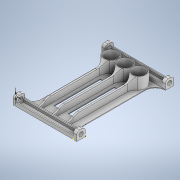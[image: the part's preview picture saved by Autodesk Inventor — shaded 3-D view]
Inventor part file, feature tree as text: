
AUTODESK INVENTOR PART (.ipt)
format: ipt  version: 2020 (Build 240168000, 168)  size: 441,856 bytes
history: native  units: mm
features: sketch x21, extrude x18, fillet x7
ambient origin geometry x8: Origin, YZ Plane, XZ Plane, XY Plane, X Axis, Y Axis, Z Axis, Center Point
bodies: Solid1 (feature_tree)
feature tree (46):
  extrude  "Extrusion1"  Depth=25.4mm
  extrude  "Extrusion2"  Depth=10.0mm TaperAngle=0.0deg
  sketch  "Sketch3"  dims[d5=2.0mm d6=190.0mm d7=0.0mm]
  extrude  "Extrusion3"  Depth=2.0mm TaperAngle=0.0deg
  extrude  "Extrusion4"  Depth=2.0mm
  fillet  "Fillet1"  Radius=8.75mm
  fillet  "Fillet2"  Radius=2.0mm
  sketch  "Sketch6"  dims[d16=2.0mm d17=290.0mm d18=0.0mm]
  extrude  "Extrusion5"  Depth=2.0mm
  sketch  "Sketch8"  dims[d22=10.0mm d23=0.0mm d24=10.0mm d25=0.0mm d26=8.75mm]
  extrude  "Extrusion6"  Depth=2.0mm TaperAngle=0.0deg
  extrude  "Extrusion7"  Depth=25.4mm
  fillet  "Fillet3"  Radius=12.7mm
  extrude  "Extrusion8"  Depth=10.0mm TaperAngle=0.0deg
  fillet  "Fillet4"  Radius=8.75mm
  extrude  "Extrusion9"  Depth=8.75mm TaperAngle=0.0deg
  extrude  "Extrusion10"  Depth=2.0mm
  extrude  "Extrusion11"  Depth=13.0mm
  extrude  "Extrusion12"  Depth=38.0mm
  extrude  "Extrusion13"  Depth=38.0mm
  fillet  "Fillet5"  Radius=30.0mm
  extrude  "Extrusion14"  Depth=35.0mm TaperAngle=0.0deg
  fillet  "Fillet6"  [1 undecoded]
  extrude  "Extrusion15"  TaperAngle=90.0deg  [1 undecoded]
  extrude  "Extrusion16"  Depth=2.0mm
  fillet  "Fillet7"  Radius=5.0mm
  extrude  "Extrusion17"  Depth=20.0mm TaperAngle=0.0deg
  extrude  "Extrusion18"  Depth=25.0mm TaperAngle=0.0deg
  sketch  "Sketch1"  dims[d0=25.4mm d1=25.4mm]
  sketch  "Sketch2"  dims[d2=12.7mm d3=10.0mm d4=0.0mm]
  sketch  "Sketch4"  dims[d8=10.0mm d9=0.0mm d10=5.0mm d11=8.75mm d12=0.0mm d13=2.0mm]
  sketch  "Sketch5"  dims[d14=8.75mm d15=2.0mm]
  sketch  "Sketch7"  dims[d19=25.4mm d20=25.4mm d21=12.7mm]
  sketch  "Sketch9"  dims[d27=5.0mm d28=8.75mm d29=0.0mm]
  sketch  "Sketch10"  dims[d30=2.0mm d31=13.0mm]
  sketch  "Sketch11"  dims[d32=190.0mm d33=0.0mm d34=13.0mm]
  sketch  "Sketch12"  dims[d35=190.0mm d36=0.0mm d37=38.0mm]
  sketch  "Sketch13"  dims[d38=38.0mm d39=38.0mm d40=30.0mm]
  sketch  "Sketch14"  dims[d41=30.0mm d42=35.0mm d43=0.0mm d44=90.0deg]
  sketch  "Sketch15"  dims[d45=90.0deg d46=90.0deg]
  sketch  "Sketch16"  dims[d47=2.0mm d48=0.0mm d49=5.0mm d50=5.0mm]
  sketch  "Sketch17"  dims[d51=5.0mm d52=20.0mm d53=0.0mm]
  sketch  "Sketch18"  dims[d54=25.0mm d55=89.0mm d56=0.0mm]
  sketch  "Sketch19"  dims[d57=25.0mm]
  sketch  "Sketch20"  dims[d58=37.0mm]
  sketch  "Sketch21"  dims[d59=37.0mm d60=20.0mm d61=0.0mm d62=5.0mm d63=5.0mm d64=8.75mm d65=0.0mm d66=2.0mm d67=38.55mm d68=38.55mm d69=38.55mm d70=35.0mm d71=0.0mm d72=17.0mm d73=17.0mm d74=2.0mm d75=0.0mm]
note: 2 required parameter values undecoded (feature->parameter linkage not recoverable at this tier; creation-order binding heuristic only, values carry confidence <= 0.55)
